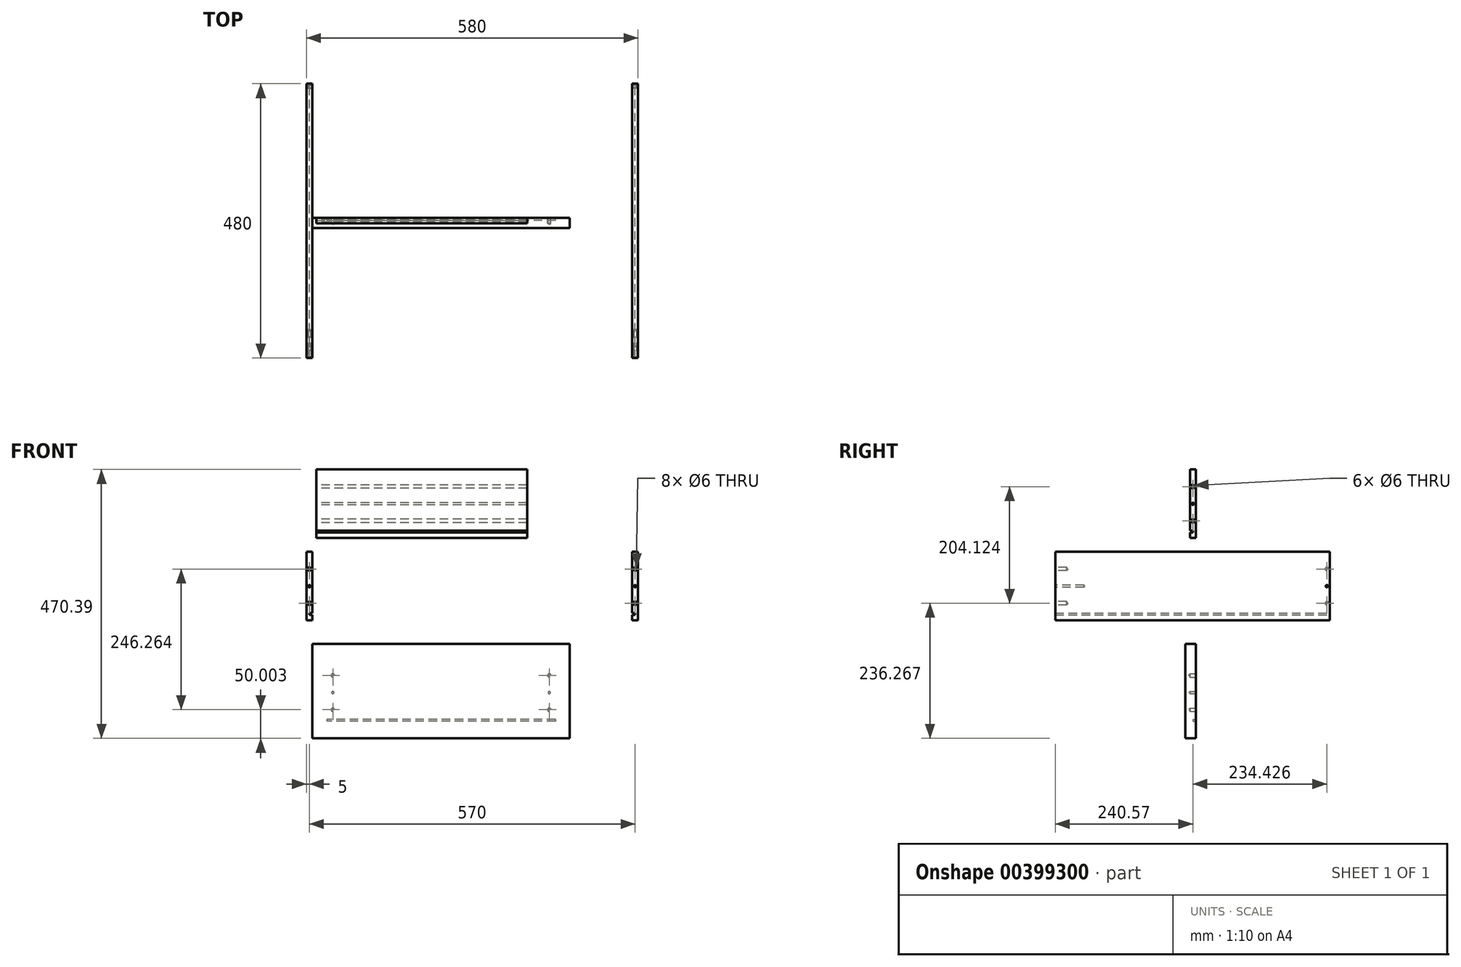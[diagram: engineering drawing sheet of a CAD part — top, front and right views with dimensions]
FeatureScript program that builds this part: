
annotation { "Feature Type Name" : "Feature", "Feature Type Description" : "" }
export const myFeature = defineFeature(function(context is Context, id is Id, definition is map)
    precondition{}
    {
        {
            var Q0;
            Q0=qCreatedBy(makeId("Front.planeOp"),FACE);
            var sketch = newSketch(context, id + "F0", { "sketchPlane" : qUnion([Q0])});
            skLineSegment(sketch, "E0", {"start": v(553.87, 203.2) * mm, "end": v(553.87, 200.2) * mm});
            skText(sketch, "E1", { "text": "Grubość Rowka", "fontName": "OpenSans-Regular.ttf"});
            const initialGuessF0  = {"E1": [0.56755, 0.19197, 1, 0, 0.02]};
            skSetInitialGuess(sketch, initialGuessF0);
            skSolve(sketch);
        }
        {
            var Q0;
            Q0=qCreatedBy(makeId("Right.planeOp"),FACE);
            var sketch = newSketch(context, id + "F1", { "sketchPlane" : qUnion([Q0])});
            skLineSegment(sketch, "E2.bottom", {"start": v(-245.57, 66.34) * mm, "end": v(234.43, 66.34) * mm});
            skLineSegment(sketch, "E2.top", {"start": v(-245.57, -53.66) * mm, "end": v(234.43, -53.66) * mm});
            skLineSegment(sketch, "E2.left", {"start": v(-245.57, 66.34) * mm, "end": v(-245.57, -53.66) * mm});
            skLineSegment(sketch, "E2.right", {"start": v(234.43, 66.34) * mm, "end": v(234.43, -53.66) * mm});
            skSolve(sketch);
        }
        {
            var Q0;
            Q0=qSketchRegion(id+"F1",true);
            extrude(context, id + "F2", {"entities" : qUnion([Q0]), "depth" : -290 * mm, "hasSecondDirection" : true, "secondDirectionOppositeDirection" : true, "secondDirectionDepth" : 280 * mm});
        }
        {
            var Q0;
            Q0=qCreatedBy(makeId("Right.planeOp"),FACE);
            var sketch = newSketch(context, id + "F3", { "sketchPlane" : qUnion([Q0])});
            skLineSegment(sketch, "E3.bottom", {"start": v(-245.57, -40.66) * mm, "end": v(234.43, -40.66) * mm});
            skLineSegment(sketch, "E3.top", {"start": v(-245.57, -43.66) * mm, "end": v(234.43, -43.66) * mm});
            skLineSegment(sketch, "E3.left", {"start": v(-245.57, -40.66) * mm, "end": v(-245.57, -43.66) * mm});
            skLineSegment(sketch, "E3.right", {"start": v(234.43, -40.66) * mm, "end": v(234.43, -43.66) * mm});
            skSolve(sketch);
        }
        {
            var Q0;
            Q0=qSketchRegion(id+"F3",true);
            var Q1;
            Q1=makeQuery(id+"F2.opExtrude","CAP_FACE",FACE,{"disambiguationData":[OSD([sQuery(id+"F1.wireOp",EDGE,"E2.bottom"),sQuery(id+"F1.wireOp",EDGE,"E2.top"),sQuery(id+"F1.wireOp",EDGE,"E2.left"),sQuery(id+"F1.wireOp",EDGE,"E2.right")])],"isStart":false});
            extrude(context, id + "F4", {"entities" : qUnion([Q0]), "endBoundEntityFace" : qUnion([Q1]), "depth" : -285 * mm, "hasSecondDirection" : true, "secondDirectionOppositeDirection" : false, "secondDirectionDepth" : -280 * mm});
        }
        {
            var Q0;
            Q0=makeQuery(id+"F4.opExtrude","SWEPT_BODY",BODY,{"disambiguationData":[OSD([sQuery(id+"F3.wireOp",EDGE,"E3.bottom"),sQuery(id+"F3.wireOp",EDGE,"E3.top"),sQuery(id+"F3.wireOp",EDGE,"E3.left"),sQuery(id+"F3.wireOp",EDGE,"E3.right")])]});
            var Q1;
            Q1=makeQuery(id+"F2.opExtrude","SWEPT_BODY",BODY,{"disambiguationData":[OSD([sQuery(id+"F1.wireOp",EDGE,"E2.bottom"),sQuery(id+"F1.wireOp",EDGE,"E2.top"),sQuery(id+"F1.wireOp",EDGE,"E2.left"),sQuery(id+"F1.wireOp",EDGE,"E2.right")])]});
            booleanBodies(context, id + "F5", {"operationType" : BooleanOperationType.SUBTRACTION, "tools" : qUnion([Q0]), "targets" : qUnion([Q1])});
        }
        {
            var Q0;
            Q0=qCreatedBy(makeId("Front.planeOp"),FACE);
            var sketch = newSketch(context, id + "F6", { "sketchPlane" : qUnion([Q0])});
            skLineSegment(sketch, "E4.bottom", {"start": v(-272.58, 210.46) * mm, "end": v(96.02, 210.46) * mm});
            skLineSegment(sketch, "E4.top", {"start": v(-272.58, 90.46) * mm, "end": v(96.02, 90.46) * mm});
            skLineSegment(sketch, "E4.left", {"start": v(-272.58, 210.46) * mm, "end": v(-272.58, 90.46) * mm});
            skLineSegment(sketch, "E4.right", {"start": v(96.02, 210.46) * mm, "end": v(96.02, 90.46) * mm});
            skSolve(sketch);
        }
        {
            var Q0;
            Q0=qCreatedBy(makeId("Front.planeOp"),FACE);
            var sketch = newSketch(context, id + "F7", { "sketchPlane" : qUnion([Q0])});
            skLineSegment(sketch, "E5.bottom", {"start": v(-272.58, 103.46) * mm, "end": v(96.02, 103.46) * mm});
            skLineSegment(sketch, "E5.top", {"start": v(-272.58, 100.46) * mm, "end": v(96.02, 100.46) * mm});
            skLineSegment(sketch, "E5.left", {"start": v(-272.58, 103.46) * mm, "end": v(-272.58, 100.46) * mm});
            skLineSegment(sketch, "E5.right", {"start": v(96.02, 103.46) * mm, "end": v(96.02, 100.46) * mm});
            skSolve(sketch);
        }
        {
            var Q0;
            Q0=qSketchRegion(id+"F6",true);
            extrude(context, id + "F8", {"entities" : qUnion([Q0]), "depth" : 10 * mm});
        }
        {
            var Q0;
            Q0=qSketchRegion(id+"F7",true);
            var Q1;
            Q1=makeQuery(id+"F8.opExtrude","SWEPT_FACE",FACE,{"disambiguationData":[OSD([sQuery(id+"F6.wireOp",EDGE,"E4.left")])]});
            extrude(context, id + "F9", {"entities" : qUnion([Q0]), "operationType" : NewBodyOperationType.REMOVE, "depth" : 10 * mm, "hasSecondDirection" : true, "secondDirectionOppositeDirection" : true, "secondDirectionBoundEntityFace" : qUnion([Q1]), "secondDirectionDepth" : -5 * mm});
        }
        {
            var Q0;
            Q0=makeQuery(id+"F8.opExtrude","SWEPT_FACE",FACE,{"disambiguationData":[OSD([sQuery(id+"F6.wireOp",EDGE,"E4.left")])]});
            var sketch = newSketch(context, id + "F10", { "sketchPlane" : qUnion([Q0])});
            skLineSegment(sketch, "E6", {"start": v(0, 198.64) * mm, "end": v(10, 198.64) * mm, "construction": true});
            skPoint(sketch, "E7", {"position": v(5, 198.64) * mm});
            skLineSegment(sketch, "E8", {"start": v(5, 210.46) * mm, "end": v(5, 90.46) * mm});
            skPoint(sketch, "E9", {"position": v(5, 180.46) * mm});
            skPoint(sketch, "E10", {"position": v(5, 120.46) * mm});
            skPoint(sketch, "E11", {"position": v(5, 150.46) * mm});
            skSolve(sketch);
        }
        {
            var Q0;
            Q0=sQuery(id+"F10.wireOp",VERTEX,"E9");
            var Q1;
            Q1=sQuery(id+"F10.wireOp",VERTEX,"E10");
            var Q2;
            Q2=makeQuery(id+"F8.opExtrude","SWEPT_BODY",BODY,{"disambiguationData":[OSD([sQuery(id+"F6.wireOp",EDGE,"E4.bottom"),sQuery(id+"F6.wireOp",EDGE,"E4.top"),sQuery(id+"F6.wireOp",EDGE,"E4.left"),sQuery(id+"F6.wireOp",EDGE,"E4.right")])]});
            hole(context, id + "F11", {"style" : HoleStyle.SIMPLE, "endStyle" : HoleEndStyle.THROUGH, "holeDiameter" : 6 * mm, "isTappedThrough" : true, "tappedDepth" : 12 * mm, "tapClearance" : 3, "startFromSketch" : true, "locations" : qUnion([Q0, Q1]), "scope" : qUnion([Q2])});
        }
        {
            var Q0;
            Q0=sQuery(id+"F10.wireOp",VERTEX,"E11");
            var Q1;
            Q1=makeQuery(id+"F8.opExtrude","SWEPT_BODY",BODY,{"disambiguationData":[OSD([sQuery(id+"F6.wireOp",EDGE,"E4.bottom"),sQuery(id+"F6.wireOp",EDGE,"E4.top"),sQuery(id+"F6.wireOp",EDGE,"E4.left"),sQuery(id+"F6.wireOp",EDGE,"E4.right")])]});
            hole(context, id + "F12", {"style" : HoleStyle.SIMPLE, "endStyle" : HoleEndStyle.THROUGH, "holeDiameter" : 4 * mm, "isTappedThrough" : true, "tappedDepth" : 12 * mm, "tapClearance" : 3, "startFromSketch" : true, "locations" : qUnion([Q0]), "scope" : qUnion([Q1])});
        }
        {
            var Q0;
            {var subQ0=sQuery(id+"F1.wireOp",EDGE,"E2.top");var subQ1=sQuery(id+"F1.wireOp",EDGE,"E2.left");var subQ2=sQuery(id+"F1.wireOp",EDGE,"E2.right");Q0=makeQuery(id+"F5.opBoolean","SPLIT",FACE,{"disambiguationData":[TD([makeQuery(id+"F2.opExtrude","SWEPT_FACE",FACE,{"disambiguationData":[OSD([subQ0])]})])],"derivedFrom":makeQuery(id+"F2.opExtrude","CAP_FACE",FACE,{"disambiguationData":[OSD([sQuery(id+"F1.wireOp",EDGE,"E2.bottom"),subQ0,subQ1,subQ2])],"isStart":true})});}
            var sketch = newSketch(context, id + "F13", { "sketchPlane" : qUnion([Q0])});
            skLineSegment(sketch, "E12", {"start": v(229.43, 66.34) * mm, "end": v(229.43, -53.66) * mm});
            skPoint(sketch, "E13", {"position": v(229.43, 36.34) * mm});
            skPoint(sketch, "E14", {"position": v(229.43, -23.66) * mm});
            skPoint(sketch, "E15", {"position": v(229.43, 6.34) * mm});
            skSolve(sketch);
        }
        {
            var Q0;
            Q0=sQuery(id+"F13.wireOp",VERTEX,"E13");
            var Q1;
            Q1=sQuery(id+"F13.wireOp",VERTEX,"E14");
            var Q2;
            Q2=makeQuery(id+"F2.opExtrude","SWEPT_BODY",BODY,{"disambiguationData":[OSD([sQuery(id+"F1.wireOp",EDGE,"E2.bottom"),sQuery(id+"F1.wireOp",EDGE,"E2.top"),sQuery(id+"F1.wireOp",EDGE,"E2.left"),sQuery(id+"F1.wireOp",EDGE,"E2.right")])]});
            hole(context, id + "F14", {"style" : HoleStyle.SIMPLE, "endStyle" : HoleEndStyle.BLIND, "holeDiameter" : 6 * mm, "holeDepth" : 7 * mm, "isTappedThrough" : true, "tappedDepth" : 12 * mm, "tapClearance" : 3, "startFromSketch" : true, "locations" : qUnion([Q0, Q1]), "scope" : qUnion([Q2])});
        }
        {
            var Q0;
            Q0=sQuery(id+"F13.wireOp",VERTEX,"E15");
            var Q1;
            Q1=makeQuery(id+"F2.opExtrude","SWEPT_BODY",BODY,{"disambiguationData":[OSD([sQuery(id+"F1.wireOp",EDGE,"E2.bottom"),sQuery(id+"F1.wireOp",EDGE,"E2.top"),sQuery(id+"F1.wireOp",EDGE,"E2.left"),sQuery(id+"F1.wireOp",EDGE,"E2.right")])]});
            hole(context, id + "F15", {"style" : HoleStyle.SIMPLE, "endStyle" : HoleEndStyle.THROUGH, "holeDiameter" : 4 * mm, "isTappedThrough" : true, "tappedDepth" : 12 * mm, "tapClearance" : 3, "startFromSketch" : true, "locations" : qUnion([Q0]), "scope" : qUnion([Q1])});
        }
        {
            var Q0;
            Q0=makeQuery(id+"F2.opExtrude","SWEPT_FACE",FACE,{"disambiguationData":[OSD([sQuery(id+"F1.wireOp",EDGE,"E2.left")])]});
            var sketch = newSketch(context, id + "F16", { "sketchPlane" : qUnion([Q0])});
            skLineSegment(sketch, "E16", {"start": v(-285, 66.34) * mm, "end": v(-285, -53.66) * mm});
            skPoint(sketch, "E17", {"position": v(-285, 36.34) * mm});
            skPoint(sketch, "E18", {"position": v(-285, 6.34) * mm});
            skPoint(sketch, "E19", {"position": v(-285, -23.66) * mm});
            skSolve(sketch);
        }
        {
            var Q0;
            Q0=sQuery(id+"F16.wireOp",VERTEX,"E17");
            var Q1;
            Q1=sQuery(id+"F16.wireOp",VERTEX,"E19");
            var Q2;
            Q2=makeQuery(id+"F2.opExtrude","SWEPT_BODY",BODY,{"disambiguationData":[OSD([sQuery(id+"F1.wireOp",EDGE,"E2.bottom"),sQuery(id+"F1.wireOp",EDGE,"E2.top"),sQuery(id+"F1.wireOp",EDGE,"E2.left"),sQuery(id+"F1.wireOp",EDGE,"E2.right")])]});
            hole(context, id + "F17", {"style" : HoleStyle.SIMPLE, "endStyle" : HoleEndStyle.BLIND, "holeDiameter" : 6 * mm, "holeDepth" : 20 * mm, "isTappedThrough" : true, "tappedDepth" : 12 * mm, "tapClearance" : 3, "startFromSketch" : true, "locations" : qUnion([Q0, Q1]), "scope" : qUnion([Q2])});
        }
        {
            var Q0;
            Q0=sQuery(id+"F16.wireOp",VERTEX,"E18");
            var Q1;
            Q1=makeQuery(id+"F2.opExtrude","SWEPT_BODY",BODY,{"disambiguationData":[OSD([sQuery(id+"F1.wireOp",EDGE,"E2.bottom"),sQuery(id+"F1.wireOp",EDGE,"E2.top"),sQuery(id+"F1.wireOp",EDGE,"E2.left"),sQuery(id+"F1.wireOp",EDGE,"E2.right")])]});
            hole(context, id + "F18", {"style" : HoleStyle.SIMPLE, "endStyle" : HoleEndStyle.BLIND, "holeDiameter" : 4 * mm, "holeDepth" : 50 * mm, "isTappedThrough" : true, "tappedDepth" : 12 * mm, "tapClearance" : 3, "startFromSketch" : true, "locations" : qUnion([Q0]), "scope" : qUnion([Q1])});
        }
        {
            var Q0;
            Q0=makeQuery(id+"F2.opExtrude","SWEPT_BODY",BODY,{"disambiguationData":[OSD([sQuery(id+"F1.wireOp",EDGE,"E2.bottom"),sQuery(id+"F1.wireOp",EDGE,"E2.top"),sQuery(id+"F1.wireOp",EDGE,"E2.left"),sQuery(id+"F1.wireOp",EDGE,"E2.right")])]});
            var Q1;
            Q1=qCreatedBy(makeId("Right.planeOp"),FACE);
            mirror(context, id + "F19", {"entities" : qUnion([Q0]), "mirrorPlane" : qUnion([Q1])});
        }
        {
            var Q0;
            Q0=qCreatedBy(makeId("Front.planeOp"),FACE);
            var sketch = newSketch(context, id + "F20", { "sketchPlane" : qUnion([Q0])});
            skLineSegment(sketch, "E20.bottom", {"start": v(-279.57, -94.93) * mm, "end": v(170.43, -94.93) * mm});
            skLineSegment(sketch, "E20.top", {"start": v(-279.57, -259.93) * mm, "end": v(170.43, -259.93) * mm});
            skLineSegment(sketch, "E20.left", {"start": v(-279.57, -94.93) * mm, "end": v(-279.57, -259.93) * mm});
            skLineSegment(sketch, "E20.right", {"start": v(170.43, -94.93) * mm, "end": v(170.43, -259.93) * mm});
            skSolve(sketch);
        }
        {
            var Q0;
            Q0=makeQuery(id+"F20.imprint","IMPRINT",FACE,{"disambiguationData":[TD([[makeQuery(id+"F20.imprint","IMPRINT",EDGE,{"derivedFrom":sQuery(id+"F20.wireOp",EDGE,"E20.bottom")}),-1.0]])]});
            var sketch = newSketch(context, id + "F21", { "sketchPlane" : qUnion([Q0])});
            skLineSegment(sketch, "E21.bottom", {"start": v(-279.57, -226.93) * mm, "end": v(170.43, -226.93) * mm, "construction": true});
            skLineSegment(sketch, "E21.top", {"start": v(-279.57, -229.93) * mm, "end": v(170.43, -229.93) * mm, "construction": true});
            skLineSegment(sketch, "E21.left", {"start": v(-279.57, -226.93) * mm, "end": v(-279.57, -229.93) * mm, "construction": true});
            skLineSegment(sketch, "E21.right", {"start": v(170.43, -226.93) * mm, "end": v(170.43, -229.93) * mm, "construction": true});
            skLineSegment(sketch, "E22.bottom", {"start": v(145.43, -226.93) * mm, "end": v(-254.57, -226.93) * mm});
            skLineSegment(sketch, "E22.top", {"start": v(145.43, -229.93) * mm, "end": v(-254.57, -229.93) * mm});
            skLineSegment(sketch, "E22.left", {"start": v(145.43, -226.93) * mm, "end": v(145.43, -229.93) * mm});
            skLineSegment(sketch, "E22.right", {"start": v(-254.57, -226.93) * mm, "end": v(-254.57, -229.93) * mm});
            skSolve(sketch);
        }
        {
            var Q0;
            Q0=qSketchRegion(id+"F20",true);
            extrude(context, id + "F22", {"entities" : qUnion([Q0]), "depth" : 18 * mm});
        }
        {
            var Q0;
            Q0=qSketchRegion(id+"F21",true);
            extrude(context, id + "F23", {"entities" : qUnion([Q0]), "operationType" : NewBodyOperationType.REMOVE, "depth" : 5 * mm});
        }
        {
            var Q0;
            {var subQ0=sQuery(id+"F20.wireOp",EDGE,"E20.bottom");var subQ1=sQuery(id+"F20.wireOp",EDGE,"E20.right");var subQ2=sQuery(id+"F20.wireOp",EDGE,"E20.left");Q0=makeQuery(id+"F23.boolean.opBoolean","SPLIT",FACE,{"disambiguationData":[TD([makeQuery(id+"F22.opExtrude","SWEPT_FACE",FACE,{"disambiguationData":[OSD([subQ0])]})])],"derivedFrom":makeQuery(id+"F22.opExtrude","CAP_FACE",FACE,{"disambiguationData":[OSD([subQ0,sQuery(id+"F20.wireOp",EDGE,"E20.top"),subQ2,subQ1])],"isStart":true})});}
            var sketch = newSketch(context, id + "F24", { "sketchPlane" : qUnion([Q0])});
            skLineSegment(sketch, "E23", {"start": v(243.87, -94.93) * mm, "end": v(243.87, -259.93) * mm, "construction": true});
            skPoint(sketch, "E24", {"position": v(243.87, -149.93) * mm});
            skPoint(sketch, "E25", {"position": v(243.87, -179.93) * mm});
            skPoint(sketch, "E26", {"position": v(243.87, -209.93) * mm});
            skLineSegment(sketch, "E27", {"start": v(54.57, -94.93) * mm, "end": v(54.57, -259.26) * mm, "construction": true});
            skPoint(sketch, "E28.MirrorP", {"position": v(-134.73, -149.93) * mm});
            skLineSegment(sketch, "E29.MirrorCS", {"start": v(-134.73, -94.93) * mm, "end": v(-134.73, -259.93) * mm, "construction": true});
            skPoint(sketch, "E30.MirrorP", {"position": v(-134.73, -179.93) * mm});
            skPoint(sketch, "E31.MirrorP", {"position": v(-134.73, -209.93) * mm});
            skSolve(sketch);
        }
        {
            var Q0;
            Q0=sQuery(id+"F24.wireOp",VERTEX,"E28.MirrorP");
            var Q1;
            Q1=sQuery(id+"F24.wireOp",VERTEX,"E31.MirrorP");
            var Q2;
            Q2=sQuery(id+"F24.wireOp",VERTEX,"E26");
            var Q3;
            Q3=sQuery(id+"F24.wireOp",VERTEX,"E24");
            var Q4;
            Q4=makeQuery(id+"F22.opExtrude","SWEPT_BODY",BODY,{"disambiguationData":[OSD([sQuery(id+"F20.wireOp",EDGE,"E20.bottom"),sQuery(id+"F20.wireOp",EDGE,"E20.top"),sQuery(id+"F20.wireOp",EDGE,"E20.left"),sQuery(id+"F20.wireOp",EDGE,"E20.right")])]});
            hole(context, id + "F25", {"style" : HoleStyle.SIMPLE, "endStyle" : HoleEndStyle.BLIND, "holeDiameter" : 6 * mm, "holeDepth" : 10 * mm, "isTappedThrough" : true, "tappedDepth" : 12 * mm, "tapClearance" : 3, "startFromSketch" : true, "locations" : qUnion([Q0, Q1, Q2, Q3]), "scope" : qUnion([Q4])});
        }
        {
            var Q0;
            Q0=sQuery(id+"F24.wireOp",VERTEX,"E30.MirrorP");
            var Q1;
            Q1=sQuery(id+"F24.wireOp",VERTEX,"E25");
            var Q2;
            Q2=makeQuery(id+"F22.opExtrude","SWEPT_BODY",BODY,{"disambiguationData":[OSD([sQuery(id+"F20.wireOp",EDGE,"E20.bottom"),sQuery(id+"F20.wireOp",EDGE,"E20.top"),sQuery(id+"F20.wireOp",EDGE,"E20.left"),sQuery(id+"F20.wireOp",EDGE,"E20.right")])]});
            hole(context, id + "F26", {"style" : HoleStyle.SIMPLE, "endStyle" : HoleEndStyle.BLIND, "holeDiameter" : 4 * mm, "holeDepth" : 10 * mm, "isTappedThrough" : true, "tappedDepth" : 12 * mm, "tapClearance" : 3, "startFromSketch" : true, "locations" : qUnion([Q0, Q1]), "scope" : qUnion([Q2])});
        }
    });
